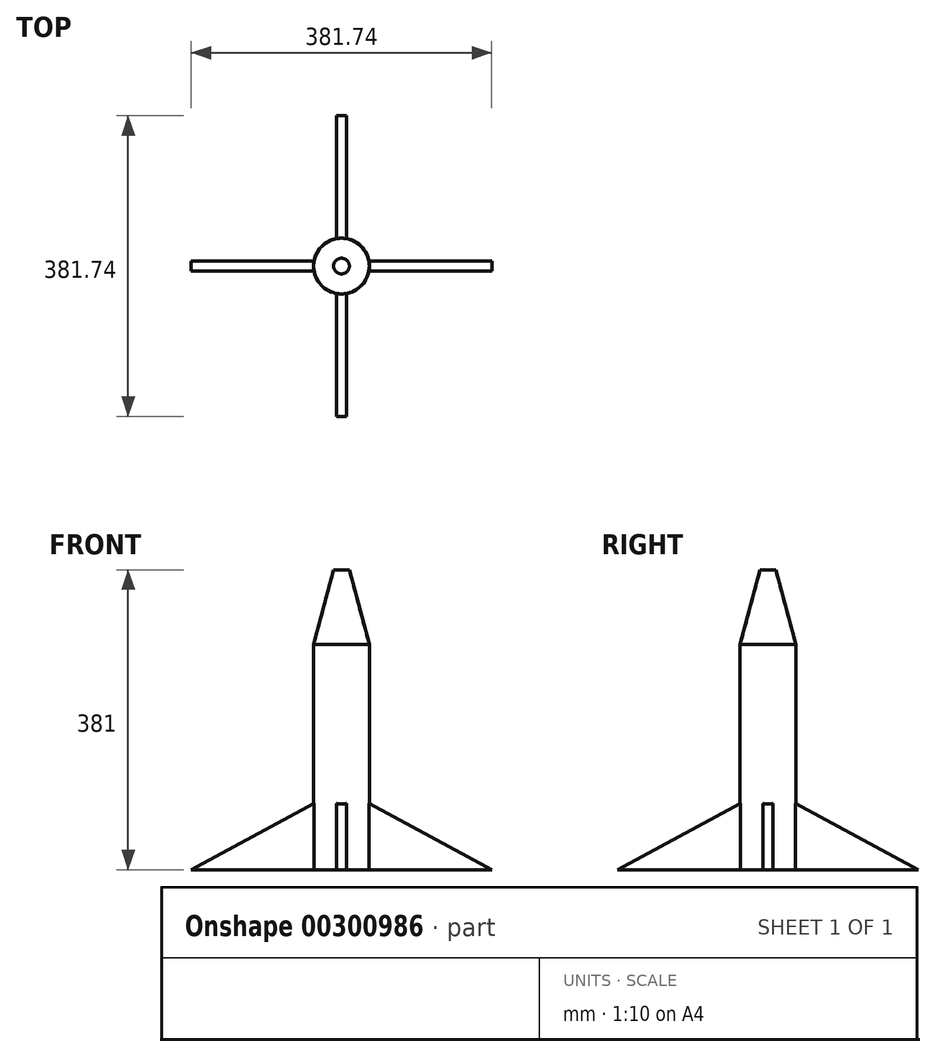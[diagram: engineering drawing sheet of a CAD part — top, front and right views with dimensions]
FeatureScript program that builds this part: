
annotation { "Feature Type Name" : "Feature", "Feature Type Description" : "" }
export const myFeature = defineFeature(function(context is Context, id is Id, definition is map)
    precondition{}
    {
        {
            var Q0;
            Q0=qCreatedBy(makeId("Top.planeOp"),FACE);
            var sketch = newSketch(context, id + "F0", { "sketchPlane" : qUnion([Q0])});
            skCircle(sketch, "E0", {"center": v(0, 0) * mm, "radius": 35.38 * mm});
            skSolve(sketch);
        }
        {
            var Q0;
            Q0 = qSketchRegion(id + "F0", true);
            extrude(context, id + "F1", {"entities" : qUnion([Q0]), "depth" : 381 * mm});
        }
        {
            var Q0;
            Q0=makeQuery(id+"F1.opExtrude","CAP_EDGE",EDGE,{"disambiguationData":[OSD([sQuery(id+"F0.wireOp",EDGE,"E0")])],"isStart":false});
            chamfer(context, id + "F2", {"entities" : qUnion([Q0]), "chamferType" : ChamferType.OFFSET_ANGLE, "width" : 25.4 * mm, "oppositeDirection" : false, "angle" : 75 * degree, "tangentPropagation" : true});
        }
        {
            var Q0;
            Q0=qCreatedBy(makeId("Front.planeOp"),FACE);
            var sketch = newSketch(context, id + "F3", { "sketchPlane" : qUnion([Q0])});
            skLineSegment(sketch, "E1", {"start": v(0, 102.74) * mm, "end": v(0, 0) * mm});
            skLineSegment(sketch, "E2", {"start": v(0, 0) * mm, "end": v(190.87, 0) * mm});
            skLineSegment(sketch, "E3", {"start": v(190.87, 0) * mm, "end": v(0, 102.74) * mm});
            skSolve(sketch);
        }
        {
            var Q0;
            Q0 = qSketchRegion(id + "F3", true);
            extrude(context, id + "F4", {"entities" : qUnion([Q0]), "operationType" : NewBodyOperationType.ADD, "endBound" : BoundingType.SYMMETRIC, "depth" : 12.7 * mm});
        }
        {
            var Q0;
            Q0=makeQuery(id+"F1.opExtrude","SWEPT_BODY",BODY,{"disambiguationData":[OSD([sQuery(id+"F0.wireOp",EDGE,"E0")])]});
            var Q1;
            Q1=makeQuery(id+"F1.opExtrude","SWEPT_FACE",FACE,{"disambiguationData":[OSD([sQuery(id+"F0.wireOp",EDGE,"E0")])]});
            circularPattern(context, id + "F5", {"entities" : qUnion([Q0]), "axis" : qUnion([Q1]), "angle" : 360 * degree, "instanceCount" : 4, "equalSpace" : true});
        }
    });
